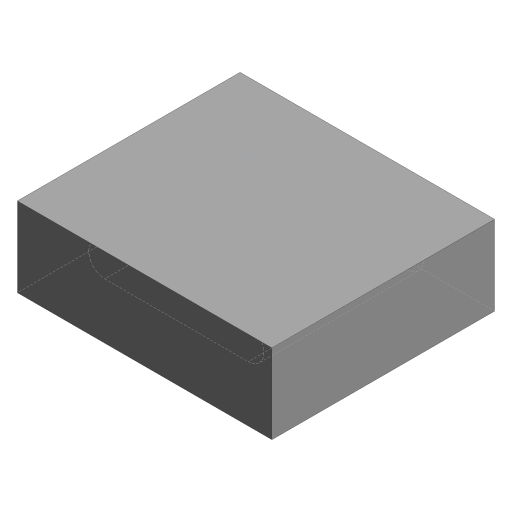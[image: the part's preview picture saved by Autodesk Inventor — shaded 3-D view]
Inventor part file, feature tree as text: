
AUTODESK INVENTOR PART (.ipt)
format: ipt  version: 2023 (Build 270158000, 158)  size: 71,680 bytes
history: native  units: mm (DEFAULTED — no unit token found)
features: sketch x2, extrude x2
ambient origin geometry x8: Origin, YZ Plane, XZ Plane, XY Plane, X Axis, Y Axis, Z Axis, Center Point
bodies: Solid1 (feature_tree)
feature tree (4):
  sketch  "Sketch1"  dims[d0=-15.875mm d1=-22.225mm d2=44.45mm d3=0.0mm]
  extrude  "Extrusion1"  Depth=44.45mm TaperAngle=0.0deg
  extrude  "Extrusion2"  [1 undecoded]
  sketch  "Sketch2"  dims[d4=31.75mm d5=0.0mm]
note: 1 required parameter value undecoded (feature->parameter linkage not recoverable at this tier; creation-order binding heuristic only, values carry confidence <= 0.55)
